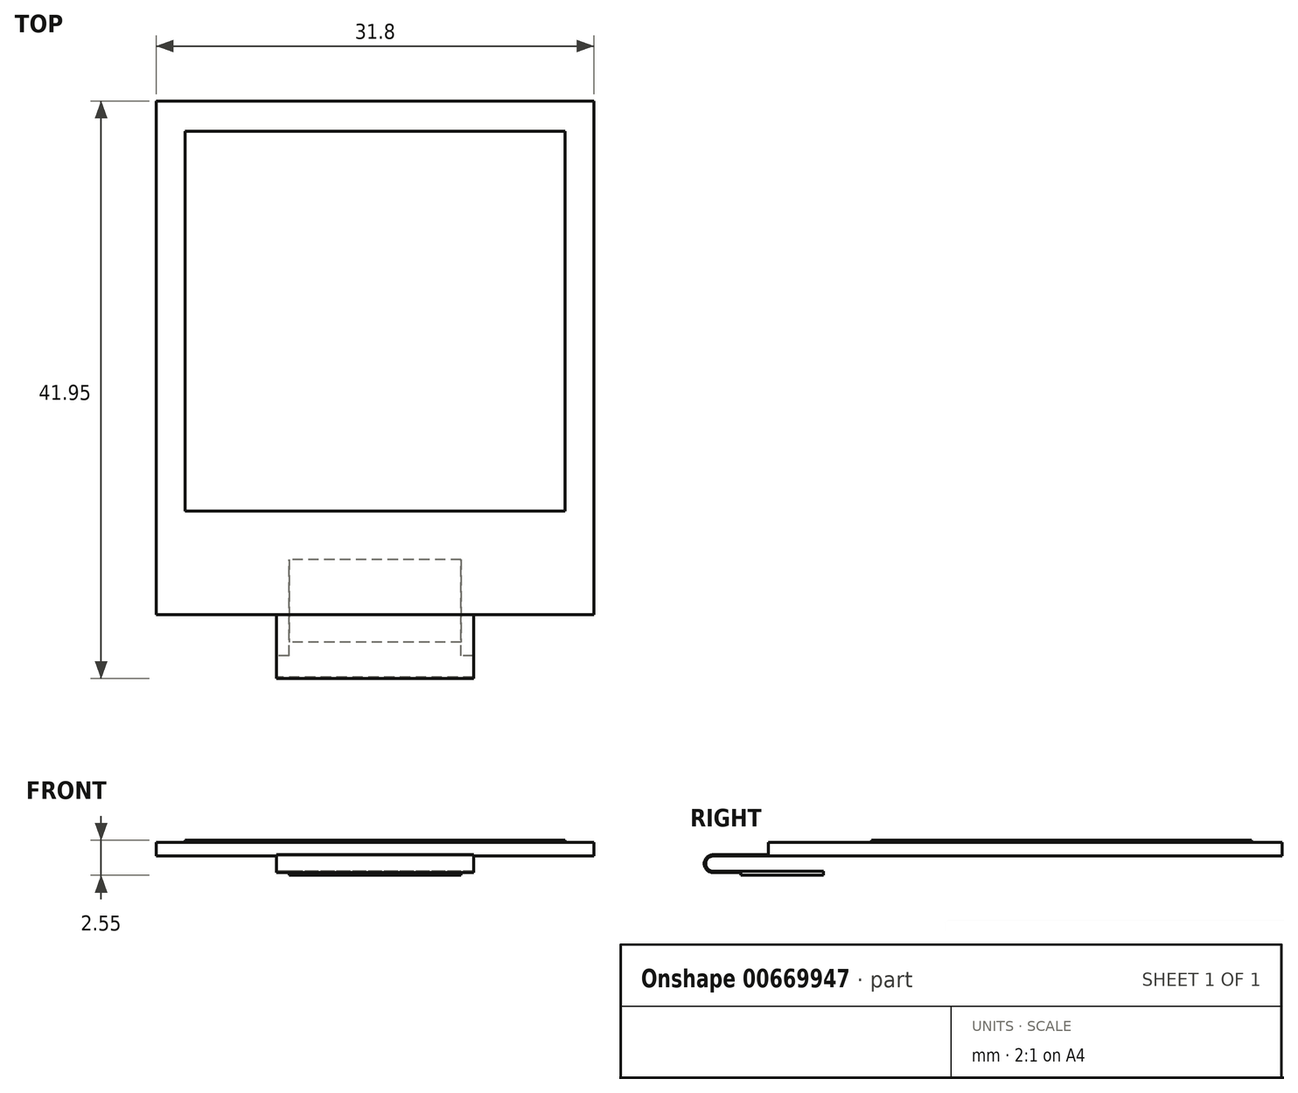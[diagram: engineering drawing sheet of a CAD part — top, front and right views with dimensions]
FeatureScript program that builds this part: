
annotation { "Feature Type Name" : "Feature", "Feature Type Description" : "" }
export const myFeature = defineFeature(function(context is Context, id is Id, definition is map)
    precondition{}
    {
        {
            var Q0;
            Q0=qCreatedBy(makeId("Right.planeOp"),FACE);
            var sketch = newSketch(context, id + "F0", { "sketchPlane" : qUnion([Q0])});
            skLineSegment(sketch, "E0.right", {"start": v(-35.1, 0) * mm, "end": v(-35.1, 0.9) * mm});
            skPoint(sketch, "E0.middle", {"position": v(0, 0) * mm});
            skLineSegment(sketch, "E1.bottom", {"start": v(-35.1, -0.1) * mm, "end": v(-39.1, -0.1) * mm});
            skLineSegment(sketch, "E1.top", {"start": v(-35.1, 0) * mm, "end": v(-39.1, 0) * mm});
            skArc(sketch, "E2", {"start": v(-39.1, -0.1) * mm, "mid": v(-39.65, -0.65) * mm, "end": v(-39.1, -1.2) * mm});
            skArc(sketch, "E3.0", {"start": v(-39.1, 0) * mm, "mid": v(-39.75, -0.65) * mm, "end": v(-39.1, -1.3) * mm});
            skLineSegment(sketch, "E4.bottom", {"start": v(-39.1, -1.3) * mm, "end": v(-37.1, -1.3) * mm});
            skLineSegment(sketch, "E4.top", {"start": v(-39.1, -1.2) * mm, "end": v(-31.1, -1.2) * mm});
            skLineSegment(sketch, "E4.right", {"start": v(-31.1, -1.3) * mm, "end": v(-31.1, -1.2) * mm});
            skLineSegment(sketch, "E5.top", {"start": v(-31.1, -1.5) * mm, "end": v(-37.1, -1.5) * mm});
            skLineSegment(sketch, "E5.left", {"start": v(-31.1, -1.3) * mm, "end": v(-31.1, -1.5) * mm});
            skLineSegment(sketch, "E5.right", {"start": v(-37.1, -1.3) * mm, "end": v(-37.1, -1.5) * mm});
            skLineSegment(sketch, "E6.bottom", {"start": v(-35.1, 0.9) * mm, "end": v(2.2, 0.9) * mm});
            skLineSegment(sketch, "E6.top", {"start": v(-35.1, -0.1) * mm, "end": v(2.2, -0.1) * mm});
            skLineSegment(sketch, "E6.left", {"start": v(-35.1, 0.9) * mm, "end": v(-35.1, 0) * mm});
            skLineSegment(sketch, "E6.right", {"start": v(2.2, 0.9) * mm, "end": v(2.2, -0.1) * mm});
            skLineSegment(sketch, "E7.bottom", {"start": v(0, 0) * mm, "end": v(-27.6, 0) * mm});
            skLineSegment(sketch, "E7.top", {"start": v(0, 1.05) * mm, "end": v(-27.6, 1.05) * mm});
            skLineSegment(sketch, "E7.left", {"start": v(0, 0) * mm, "end": v(0, 1.05) * mm});
            skLineSegment(sketch, "E7.right", {"start": v(-27.6, 0) * mm, "end": v(-27.6, 1.05) * mm});
            skLineSegment(sketch, "E8", {"start": v(-35.1, 0) * mm, "end": v(-35.1, -0.1) * mm});
            skLineSegment(sketch, "E9", {"start": v(-38.1, -1.2) * mm, "end": v(-38.1, -1.3) * mm});
            skSolve(sketch);
        }
        {
            var Q0;
            {var subQ5=sQuery(id+"F0.wireOp",EDGE,"E7.top");Q0=makeQuery(id+"F0.imprint","IMPRINT",FACE,{"disambiguationData":[TD([[makeQuery(id+"F0.imprint","IMPRINT",EDGE,{"derivedFrom":subQ5}),1.0]])]});}
            var Q1;
            {var subQ5=sQuery(id+"F0.wireOp",EDGE,"E7.bottom");Q1=makeQuery(id+"F0.imprint","IMPRINT",FACE,{"disambiguationData":[TD([[makeQuery(id+"F0.imprint","IMPRINT",EDGE,{"derivedFrom":subQ5}),-1.0]])]});}
            extrude(context, id + "F1", {"entities" : qUnion([Q0, Q1]), "endBound" : BoundingType.SYMMETRIC, "depth" : 27.6 * mm, "offsetDistance" : 25 * mm});
        }
        {
            var Q0;
            Q0=makeQuery(id+"F0.imprint","IMPRINT",FACE,{"disambiguationData":[TD([[makeQuery(id+"F0.imprint","IMPRINT",EDGE,{"derivedFrom":sQuery(id+"F0.wireOp",EDGE,"E6.top")}),1.0]])]});
            var Q1;
            {var subQ5=sQuery(id+"F0.wireOp",EDGE,"E7.bottom");Q1=makeQuery(id+"F0.imprint","IMPRINT",FACE,{"disambiguationData":[TD([[makeQuery(id+"F0.imprint","IMPRINT",EDGE,{"derivedFrom":subQ5}),-1.0]])]});}
            extrude(context, id + "F2", {"entities" : qUnion([Q0, Q1]), "operationType" : NewBodyOperationType.ADD, "endBound" : BoundingType.SYMMETRIC, "depth" : 31.8 * mm, "offsetDistance" : 25 * mm});
        }
        {
            var Q0;
            Q0=makeQuery(id+"F0.imprint","IMPRINT",FACE,{"disambiguationData":[TD([[makeQuery(id+"F0.imprint","IMPRINT",EDGE,{"derivedFrom":sQuery(id+"F0.wireOp",EDGE,"E1.bottom")}),-1.0]])]});
            extrude(context, id + "F3", {"entities" : qUnion([Q0]), "operationType" : NewBodyOperationType.ADD, "endBound" : BoundingType.SYMMETRIC, "depth" : 14.3 * mm, "offsetDistance" : 25 * mm});
        }
        {
            var Q0;
            {var subQ0=sQuery(id+"F0.wireOp",EDGE,"E4.right");Q0=makeQuery(id+"F0.imprint","IMPRINT",FACE,{"disambiguationData":[TD([[makeQuery(id+"F0.imprint","IMPRINT",EDGE,{"derivedFrom":subQ0}),1.0]])]});}
            extrude(context, id + "F4", {"entities" : qUnion([Q0]), "operationType" : NewBodyOperationType.ADD, "endBound" : BoundingType.SYMMETRIC, "depth" : 12.5 * mm, "offsetDistance" : 25 * mm});
        }
    });
